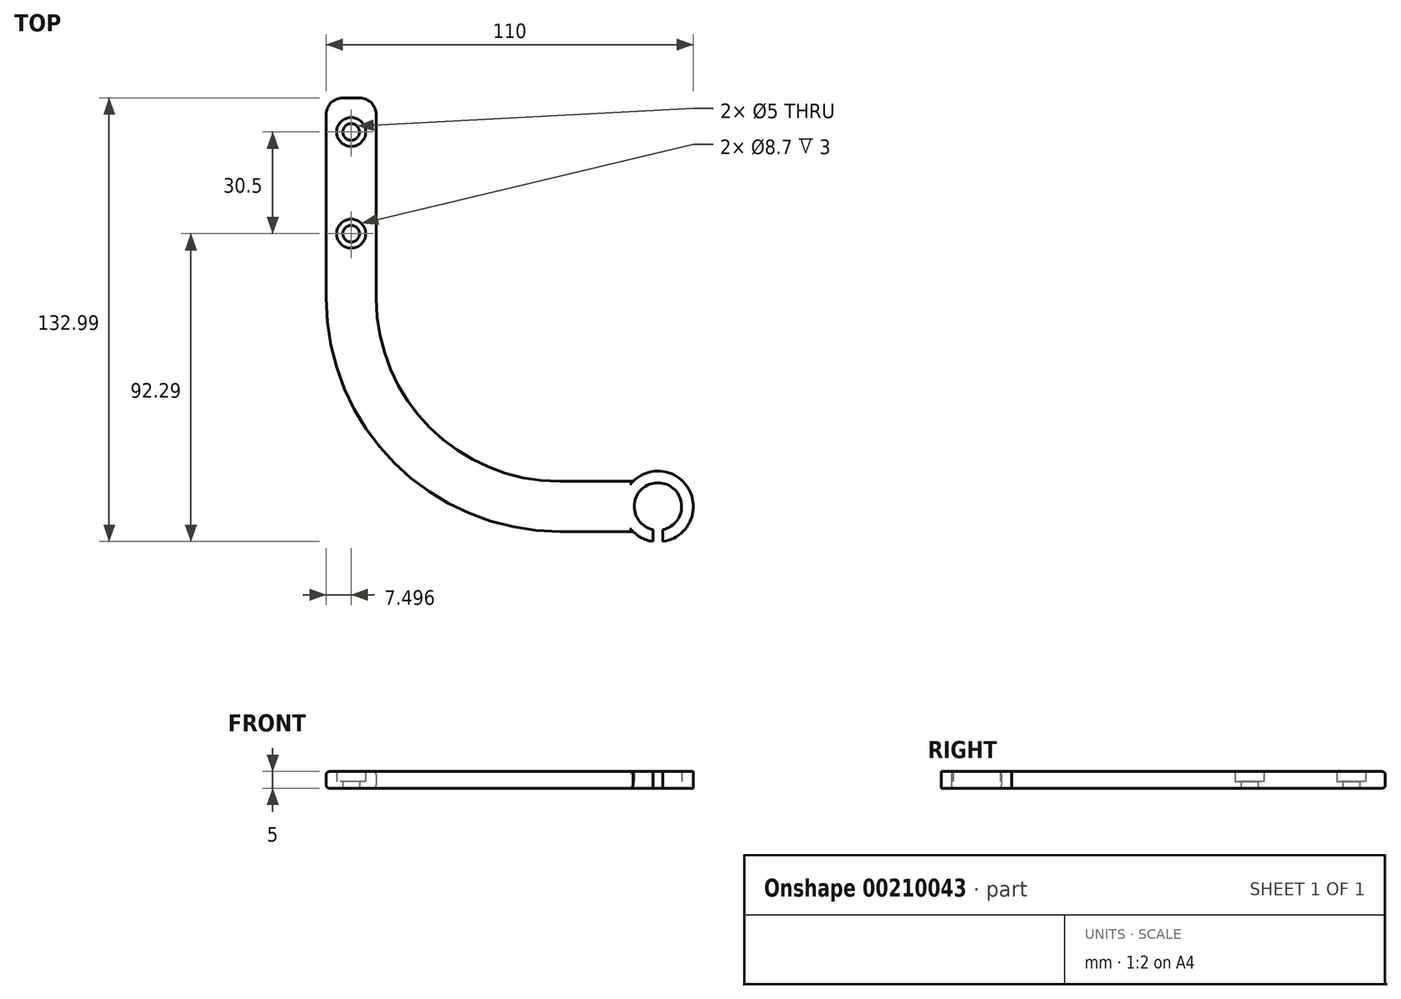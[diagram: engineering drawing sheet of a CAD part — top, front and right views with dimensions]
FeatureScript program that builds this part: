
annotation { "Feature Type Name" : "Feature", "Feature Type Description" : "" }
export const myFeature = defineFeature(function(context is Context, id is Id, definition is map)
    precondition{}
    {
        {
            var Q0;
            Q0=qCreatedBy(makeId("Top.planeOp"),FACE);
            var sketch = newSketch(context, id + "F0", { "sketchPlane" : qUnion([Q0])});
            skLineSegment(sketch, "E0.MirrorCS", {"start": v(151.6, 0.56) * mm, "end": v(148.6, 0.56) * mm, "construction": true});
            skLineSegment(sketch, "E1.MirrorCS", {"start": v(148.6, 0.56) * mm, "end": v(148.6, -3) * mm});
            skLineSegment(sketch, "E2.MirrorCS", {"start": v(151.6, 0.56) * mm, "end": v(151.6, -3) * mm});
            skPoint(sketch, "E3.MirrorP", {"position": v(58.2, 70) * mm});
            skLineSegment(sketch, "E4.MirrorCS", {"start": v(50.7, 70) * mm, "end": v(50.7, 0) * mm, "construction": true});
            skArc(sketch, "E5.MirrorCS", {"start": v(148.6, -3) * mm, "mid": v(145.37, -1.98) * mm, "end": v(142.62, 0) * mm});
            skLineSegment(sketch, "E6.MirrorCS", {"start": v(65.7, 70) * mm, "end": v(50.7, 70) * mm, "construction": true});
            skLineSegment(sketch, "E7.MirrorCS", {"start": v(142.62, 15) * mm, "end": v(142.62, 0) * mm, "construction": true});
            skLineSegment(sketch, "E8.MirrorCS", {"start": v(142.62, 0) * mm, "end": v(120.7, 0) * mm});
            skCircle(sketch, "E9.MirrorC", {"center": v(58.2, 89.3) * mm, "radius": 2.5 * mm});
            skArc(sketch, "E10.MirrorCS", {"start": v(148.6, 0.56) * mm, "mid": v(150.1, 14.6) * mm, "end": v(151.6, 0.56) * mm});
            skLineSegment(sketch, "E11.MirrorCS", {"start": v(50.7, 130) * mm, "end": v(50.7, 70) * mm});
            skArc(sketch, "E12.MirrorCS", {"start": v(142.62, 15) * mm, "mid": v(159.59, 12.24) * mm, "end": v(151.6, -3) * mm});
            skPoint(sketch, "E13.MirrorP", {"position": v(150.1, 0.56) * mm});
            skPoint(sketch, "E14.MirrorP", {"position": v(142.62, 7.5) * mm});
            skLineSegment(sketch, "E15.MirrorCS", {"start": v(65.7, 130) * mm, "end": v(50.7, 130) * mm});
            skLineSegment(sketch, "E16.MirrorCS", {"start": v(142.62, 15) * mm, "end": v(120.7, 15) * mm});
            skArc(sketch, "E17.MirrorCS", {"start": v(120.7, 15) * mm, "mid": v(81.82, 31.1) * mm, "end": v(65.7, 70) * mm});
            skCircle(sketch, "E18.MirrorC", {"center": v(58.2, 119.8) * mm, "radius": 2.5 * mm});
            skArc(sketch, "E19.MirrorCS", {"start": v(120.7, 0) * mm, "mid": v(71.2, 20.5) * mm, "end": v(50.7, 70) * mm});
            skLineSegment(sketch, "E20.MirrorCS", {"start": v(65.7, 130) * mm, "end": v(65.7, 70) * mm});
            skSolve(sketch);
        }
        {
            var Q0;
            Q0=qSketchRegion(id+"F0",true);
            extrude(context, id + "F1", {"entities" : qUnion([Q0]), "depth" : 5 * mm});
        }
        {
            var Q0;
            Q0=qCreatedBy(makeId("Top.planeOp"),FACE);
            cPlane(context, id + "F2", {"entities" : qUnion([Q0]), "cplaneType" : CPlaneType.OFFSET, "offset" : 2 * mm, "width" : 150 * mm, "height" : 150 * mm});
        }
        {
            var Q0;
            Q0=qCreatedBy(id+"F2.planeOp",FACE);
            var sketch = newSketch(context, id + "F3", { "sketchPlane" : qUnion([Q0])});
            skCircle(sketch, "E21.MirrorC", {"center": v(58.2, 119.8) * mm, "radius": 4.35 * mm});
            skCircle(sketch, "E22.MirrorC", {"center": v(58.2, 89.3) * mm, "radius": 4.35 * mm});
            skSolve(sketch);
        }
        {
            var Q0;
            Q0=qSketchRegion(id+"F3",true);
            var Q1;
            Q1=makeQuery(id+"F1.opExtrude","CAP_FACE",FACE,{"disambiguationData":[OSD([sQuery(id+"F0.wireOp",EDGE,"E1.MirrorCS"),sQuery(id+"F0.wireOp",EDGE,"E2.MirrorCS"),sQuery(id+"F0.wireOp",EDGE,"E5.MirrorCS"),sQuery(id+"F0.wireOp",EDGE,"E8.MirrorCS"),sQuery(id+"F0.wireOp",EDGE,"E9.MirrorC"),sQuery(id+"F0.wireOp",EDGE,"E10.MirrorCS"),sQuery(id+"F0.wireOp",EDGE,"E11.MirrorCS"),sQuery(id+"F0.wireOp",EDGE,"E12.MirrorCS"),sQuery(id+"F0.wireOp",EDGE,"E15.MirrorCS"),sQuery(id+"F0.wireOp",EDGE,"E16.MirrorCS"),sQuery(id+"F0.wireOp",EDGE,"E17.MirrorCS"),sQuery(id+"F0.wireOp",EDGE,"E18.MirrorC"),sQuery(id+"F0.wireOp",EDGE,"E19.MirrorCS"),sQuery(id+"F0.wireOp",EDGE,"E20.MirrorCS")])],"isStart":false});
            extrude(context, id + "F4", {"entities" : qUnion([Q0]), "operationType" : NewBodyOperationType.REMOVE, "endBound" : BoundingType.UP_TO_SURFACE, "endBoundEntityFace" : qUnion([Q1]), "depth" : 25 * mm});
        }
        {
            var Q0;
            Q0=makeQuery(id+"F1.opExtrude","SWEPT_EDGE",EDGE,{"disambiguationData":[OSD([sQuery(id+"F0.wireOp",EDGE,"NnDsAYHU-EAv2-hiKR-3vPe-xygNojttSd6l.bottom"),sQuery(id+"F0.wireOp",EDGE,"NnDsAYHU-EAv2-hiKR-3vPe-xygNojttSd6l.right")])]});
            var Q1;
            Q1=makeQuery(id+"F1.opExtrude","SWEPT_EDGE",EDGE,{"disambiguationData":[OSD([sQuery(id+"F0.wireOp",EDGE,"E11.MirrorCS"),sQuery(id+"F0.wireOp",EDGE,"E15.MirrorCS")])]});
            fillet(context, id + "F5", {"entities" : qUnion([Q0, Q1]), "radius" : 5 * mm, "tangentPropagation" : true, "allowEdgeOverflow" : false});
        }
        {
            var Q0;
            Q0=makeQuery(id+"F1.opExtrude","SWEPT_EDGE",EDGE,{"disambiguationData":[OSD([sQuery(id+"F0.wireOp",EDGE,"NnDsAYHU-EAv2-hiKR-3vPe-xygNojttSd6l.bottom"),sQuery(id+"F0.wireOp",EDGE,"NnDsAYHU-EAv2-hiKR-3vPe-xygNojttSd6l.left")])]});
            var Q1;
            Q1=makeQuery(id+"F1.opExtrude","SWEPT_EDGE",EDGE,{"disambiguationData":[OSD([sQuery(id+"F0.wireOp",EDGE,"E15.MirrorCS"),sQuery(id+"F0.wireOp",EDGE,"E20.MirrorCS")])]});
            fillet(context, id + "F6", {"entities" : qUnion([Q0, Q1]), "radius" : 5 * mm, "tangentPropagation" : true, "allowEdgeOverflow" : false});
        }
        {
            var Q0;
            Q0=makeQuery(id+"F1.opExtrude","CAP_EDGE",EDGE,{"disambiguationData":[OSD([sQuery(id+"F0.wireOp",EDGE,"NnDsAYHU-EAv2-hiKR-3vPe-xygNojttSd6l.right")])],"isStart":false});
            var Q1;
            Q1=makeQuery(id+"F1.opExtrude","CAP_EDGE",EDGE,{"disambiguationData":[OSD([sQuery(id+"F0.wireOp",EDGE,"E11.MirrorCS")])],"isStart":false});
            fillet(context, id + "F7", {"entities" : qUnion([Q0, Q1]), "radius" : 1 * mm, "tangentPropagation" : true, "allowEdgeOverflow" : false});
        }
        {
            var Q0;
            Q0=makeQuery(id+"F1.opExtrude","CAP_EDGE",EDGE,{"disambiguationData":[OSD([sQuery(id+"F0.wireOp",EDGE,"NnDsAYHU-EAv2-hiKR-3vPe-xygNojttSd6l.right")])],"isStart":true});
            var Q1;
            Q1=makeQuery(id+"F1.opExtrude","CAP_EDGE",EDGE,{"disambiguationData":[OSD([sQuery(id+"F0.wireOp",EDGE,"E11.MirrorCS")])],"isStart":true});
            fillet(context, id + "F8", {"entities" : qUnion([Q0, Q1]), "radius" : 1 * mm, "tangentPropagation" : true, "allowEdgeOverflow" : false});
        }
    });
